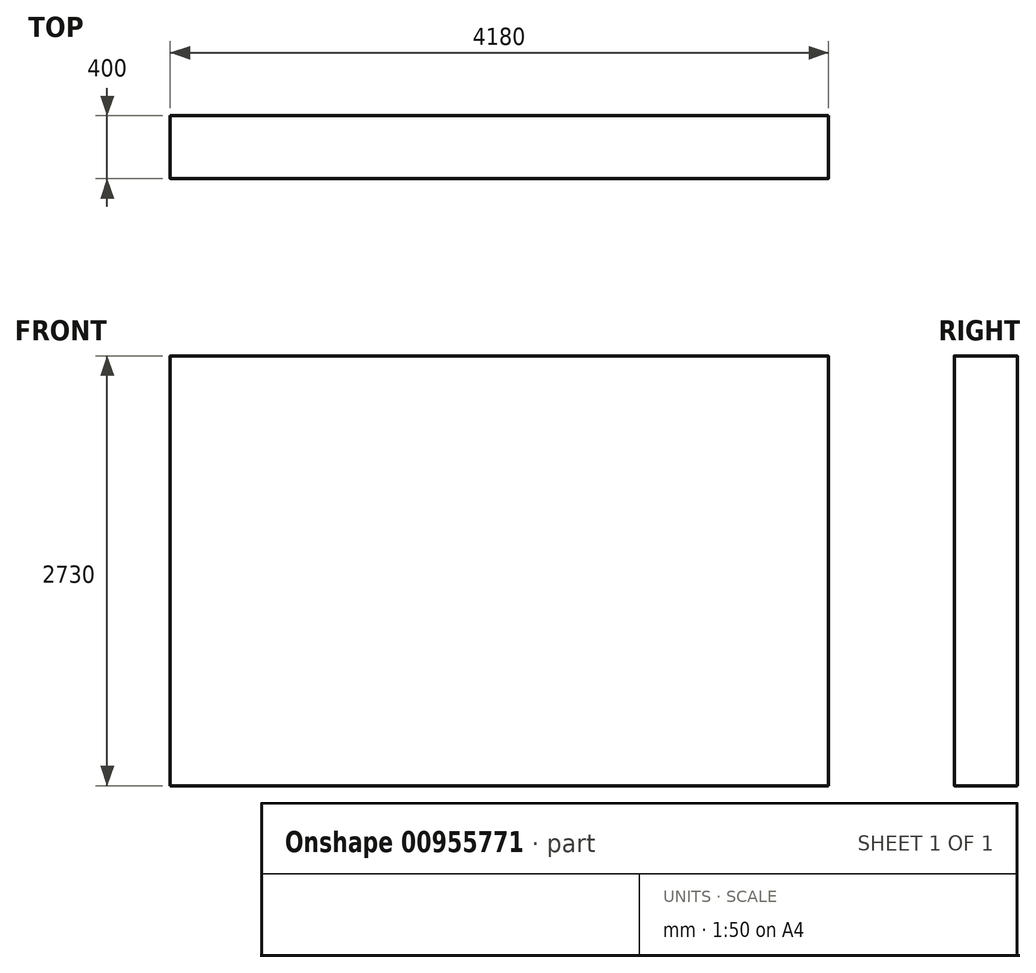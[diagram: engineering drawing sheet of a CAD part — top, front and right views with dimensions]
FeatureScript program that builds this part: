
annotation { "Feature Type Name" : "Feature", "Feature Type Description" : "" }
export const myFeature = defineFeature(function(context is Context, id is Id, definition is map)
    precondition{}
    {
        {
            var Q0;
            Q0=qCreatedBy(makeId("Front.planeOp"),FACE);
            var sketch = newSketch(context, id + "F0", { "sketchPlane" : qUnion([Q0])});
            skLineSegment(sketch, "E0.bottom", {"start": v(-1955.22, 2730) * mm, "end": v(2224.78, 2730) * mm});
            skLineSegment(sketch, "E0.top", {"start": v(-1955.22, 0) * mm, "end": v(2224.78, 0) * mm});
            skLineSegment(sketch, "E0.left", {"start": v(-1955.22, 2730) * mm, "end": v(-1955.22, 0) * mm});
            skLineSegment(sketch, "E0.right", {"start": v(2224.78, 2730) * mm, "end": v(2224.78, 0) * mm});
            skSolve(sketch);
        }
        {
            var Q0;
            Q0=makeQuery(id+"F0.imprint","IMPRINT",FACE,{"disambiguationData":[TD([[makeQuery(id+"F0.imprint","IMPRINT",EDGE,{"derivedFrom":sQuery(id+"F0.wireOp",EDGE,"E0.bottom")}),-1.0]])]});
            extrude(context, id + "F1", {"entities" : qUnion([Q0]), "depth" : 400 * mm, "offsetDistance" : 25.4 * mm});
        }
        {
            var Q0;
            Q0=makeQuery(id+"F1.opExtrude","CAP_EDGE",EDGE,{"disambiguationData":[OSD([sQuery(id+"F0.wireOp",EDGE,"E0.top")])],"isStart":false});
            fillet(context, id + "F2", {"entities" : qUnion([Q0]), "radius" : ((0.5 * sqrt(2)) / 2) * mm, "tangentPropagation" : true, "allowEdgeOverflow" : false});
        }
        {
            var Q0;
            Q0=makeQuery(id+"F1.opExtrude","CAP_EDGE",EDGE,{"disambiguationData":[OSD([sQuery(id+"F0.wireOp",EDGE,"E0.top")])],"isStart":true});
            fillet(context, id + "F3", {"entities" : qUnion([Q0]), "radius" : ((0.5 * sqrt(2)) / 2) * mm, "tangentPropagation" : true, "allowEdgeOverflow" : false});
        }
        {
            var Q0;
            Q0=makeQuery(id+"F1.opExtrude","CAP_EDGE",EDGE,{"disambiguationData":[OSD([sQuery(id+"F0.wireOp",EDGE,"E0.left")])],"isStart":true});
            fillet(context, id + "F4", {"entities" : qUnion([Q0]), "radius" : ((.5 * sqrt(2)) / 2) * mm, "tangentPropagation" : true, "allowEdgeOverflow" : false});
        }
        {
            var Q0;
            Q0=makeQuery(id+"F1.opExtrude","CAP_EDGE",EDGE,{"disambiguationData":[OSD([sQuery(id+"F0.wireOp",EDGE,"E0.right")])],"isStart":true});
            fillet(context, id + "F5", {"entities" : qUnion([Q0]), "radius" : ((.5 * sqrt(2)) / 2) * mm, "tangentPropagation" : true, "allowEdgeOverflow" : false});
        }
        {
            var Q0;
            Q0=makeQuery(id+"F1.opExtrude","CAP_EDGE",EDGE,{"disambiguationData":[OSD([sQuery(id+"F0.wireOp",EDGE,"E0.bottom")])],"isStart":true});
            fillet(context, id + "F6", {"entities" : qUnion([Q0]), "radius" : ((.5 * sqrt(2)) / 2) * mm, "tangentPropagation" : true, "allowEdgeOverflow" : false});
        }
    });
